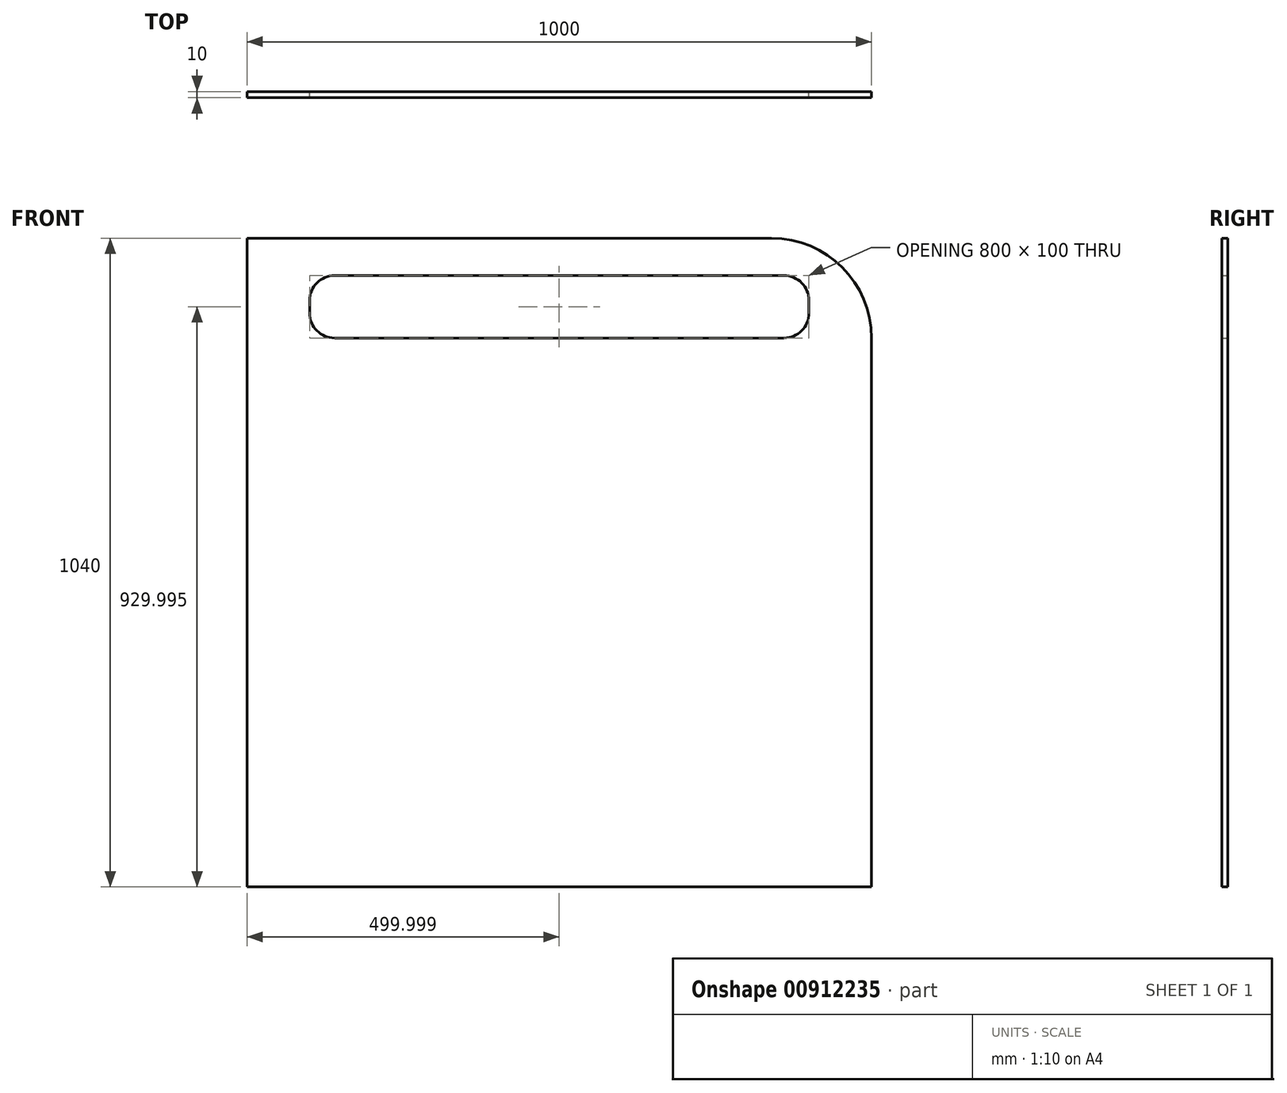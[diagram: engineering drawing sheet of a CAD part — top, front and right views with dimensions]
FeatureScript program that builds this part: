
annotation { "Feature Type Name" : "Feature", "Feature Type Description" : "" }
export const myFeature = defineFeature(function(context is Context, id is Id, definition is map)
    precondition{}
    {
        {
            var Q0;
            Q0=qCreatedBy(makeId("Front.planeOp"),FACE);
            var sketch = newSketch(context, id + "F0", { "sketchPlane" : qUnion([Q0])});
            skLineSegment(sketch, "E0.bottom", {"start": v(-491.45, 693.29) * mm, "end": v(348.55, 693.29) * mm});
            skLineSegment(sketch, "E0.top", {"start": v(-491.45, -346.71) * mm, "end": v(508.55, -346.71) * mm});
            skLineSegment(sketch, "E0.left", {"start": v(-491.45, 693.29) * mm, "end": v(-491.45, -346.71) * mm});
            skLineSegment(sketch, "E0.right", {"start": v(508.55, 533.29) * mm, "end": v(508.55, -346.71) * mm});
            skPoint(sketch, "E1.visualSharp", {"position": v(508.55, 693.29) * mm});
            skArc(sketch, "E1.filletArc", {"start": v(508.55, 533.29) * mm, "mid": v(461.69, 646.42) * mm, "end": v(348.55, 693.29) * mm});
            skLineSegment(sketch, "E2.bottom", {"start": v(-351.45, 633.29) * mm, "end": v(368.55, 633.29) * mm});
            skLineSegment(sketch, "E2.top", {"start": v(-351.45, 533.29) * mm, "end": v(368.55, 533.29) * mm});
            skLineSegment(sketch, "E2.left", {"start": v(-391.45, 593.29) * mm, "end": v(-391.45, 573.29) * mm});
            skLineSegment(sketch, "E2.right", {"start": v(408.55, 593.29) * mm, "end": v(408.55, 573.29) * mm});
            skPoint(sketch, "E3.visualSharp", {"position": v(-391.45, 633.29) * mm});
            skArc(sketch, "E3.filletArc", {"start": v(-351.45, 633.29) * mm, "mid": v(-379.74, 621.57) * mm, "end": v(-391.45, 593.29) * mm});
            skPoint(sketch, "E4.visualSharp", {"position": v(-391.45, 533.29) * mm});
            skArc(sketch, "E4.filletArc", {"start": v(-391.45, 573.29) * mm, "mid": v(-379.74, 545) * mm, "end": v(-351.45, 533.29) * mm});
            skPoint(sketch, "E5.visualSharp", {"position": v(408.55, 533.29) * mm});
            skArc(sketch, "E5.filletArc", {"start": v(368.55, 533.29) * mm, "mid": v(396.83, 545) * mm, "end": v(408.55, 573.29) * mm});
            skPoint(sketch, "E6.visualSharp", {"position": v(408.55, 633.29) * mm});
            skArc(sketch, "E6.filletArc", {"start": v(408.55, 593.29) * mm, "mid": v(396.83, 621.57) * mm, "end": v(368.55, 633.29) * mm});
            skSolve(sketch);
        }
        {
            var Q0;
            Q0 = qSketchRegion(id + "F0", true);
            extrude(context, id + "F1", {"entities" : qUnion([Q0]), "depth" : 10 * mm, "offsetDistance" : 25 * mm});
        }
    });
